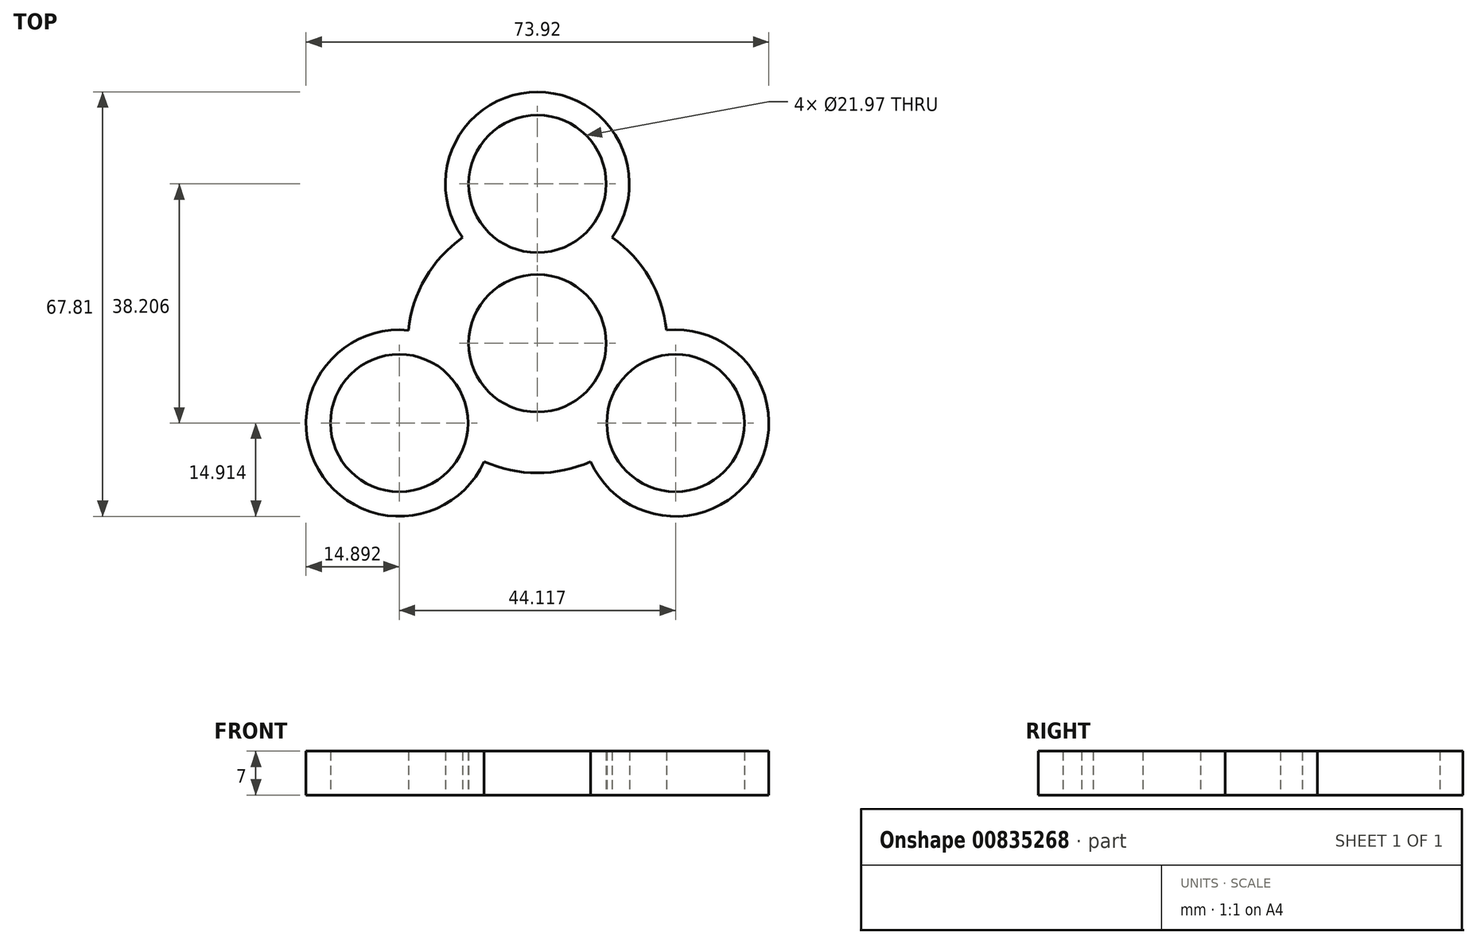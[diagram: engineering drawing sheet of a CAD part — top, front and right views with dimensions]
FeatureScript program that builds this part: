
annotation { "Feature Type Name" : "Feature", "Feature Type Description" : "" }
export const myFeature = defineFeature(function(context is Context, id is Id, definition is map)
    precondition{}
    {
        {
            var Q0;
            Q0=qCreatedBy(makeId("Top.planeOp"),FACE);
            var sketch = newSketch(context, id + "F0", { "sketchPlane" : qUnion([Q0])});
            skCircle(sketch, "E0", {"center": v(0, 0) * mm, "radius": 10.99 * mm});
            skCircle(sketch, "E1", {"center": v(0, 0) * mm, "radius": 25.47 * mm, "construction": true});
            skCircle(sketch, "E2", {"center": v(0, 25.47) * mm, "radius": 10.99 * mm});
            skCircle(sketch, "E3", {"center": v(-22.06, -12.74) * mm, "radius": 10.99 * mm});
            skCircle(sketch, "E4", {"center": v(22.06, -12.74) * mm, "radius": 10.99 * mm});
            skLineSegment(sketch, "E5", {"start": v(-22.06, -12.74) * mm, "end": v(22.06, -12.74) * mm, "construction": true});
            skLineSegment(sketch, "E6", {"start": v(0, 25.47) * mm, "end": v(-22.06, -12.74) * mm, "construction": true});
            skLineSegment(sketch, "E7", {"start": v(22.06, -12.74) * mm, "end": v(0, 25.47) * mm, "construction": true});
            skLineSegment(sketch, "E8.bottom", {"start": v(-57.15, 57.15) * mm, "end": v(57.15, 57.15) * mm, "construction": true});
            skLineSegment(sketch, "E8.top", {"start": v(-57.15, -57.15) * mm, "end": v(57.15, -57.15) * mm, "construction": true});
            skLineSegment(sketch, "E8.left", {"start": v(-57.15, 57.15) * mm, "end": v(-57.15, -57.15) * mm, "construction": true});
            skLineSegment(sketch, "E8.right", {"start": v(57.15, 57.15) * mm, "end": v(57.15, -57.15) * mm, "construction": true});
            skPoint(sketch, "E9", {"position": v(-57.15, 0) * mm});
            skPoint(sketch, "E10", {"position": v(0, 57.15) * mm});
            skArc(sketch, "E11", {"start": v(-11.94, 16.92) * mm, "mid": v(-17.88, 10.44) * mm, "end": v(-20.6, 2.08) * mm});
            skArc(sketch, "E12", {"start": v(8.48, -18.9) * mm, "mid": v(34.97, -20.2) * mm, "end": v(20.6, 2.1) * mm});
            skArc(sketch, "E13", {"start": v(-20.6, 2.08) * mm, "mid": v(-34.95, -20.18) * mm, "end": v(-8.5, -18.89) * mm});
            skArc(sketch, "E14.trimOffspring", {"start": v(11.94, 16.92) * mm, "mid": v(0, 40.16) * mm, "end": v(-11.94, 16.92) * mm});
            skArc(sketch, "E15.trimOffspring", {"start": v(20.6, 2.1) * mm, "mid": v(17.88, 10.45) * mm, "end": v(11.94, 16.92) * mm});
            skArc(sketch, "E16.trimOffspring", {"start": v(-8.5, -18.89) * mm, "mid": v(0, -20.7) * mm, "end": v(8.48, -18.9) * mm});
            skSolve(sketch);
        }
        {
            var Q0;
            Q0 = qSketchRegion(id + "F0", true);
            extrude(context, id + "F1", {"entities" : qUnion([Q0]), "depth" : 7 * mm, "offsetDistance" : 25.4 * mm});
        }
    });
